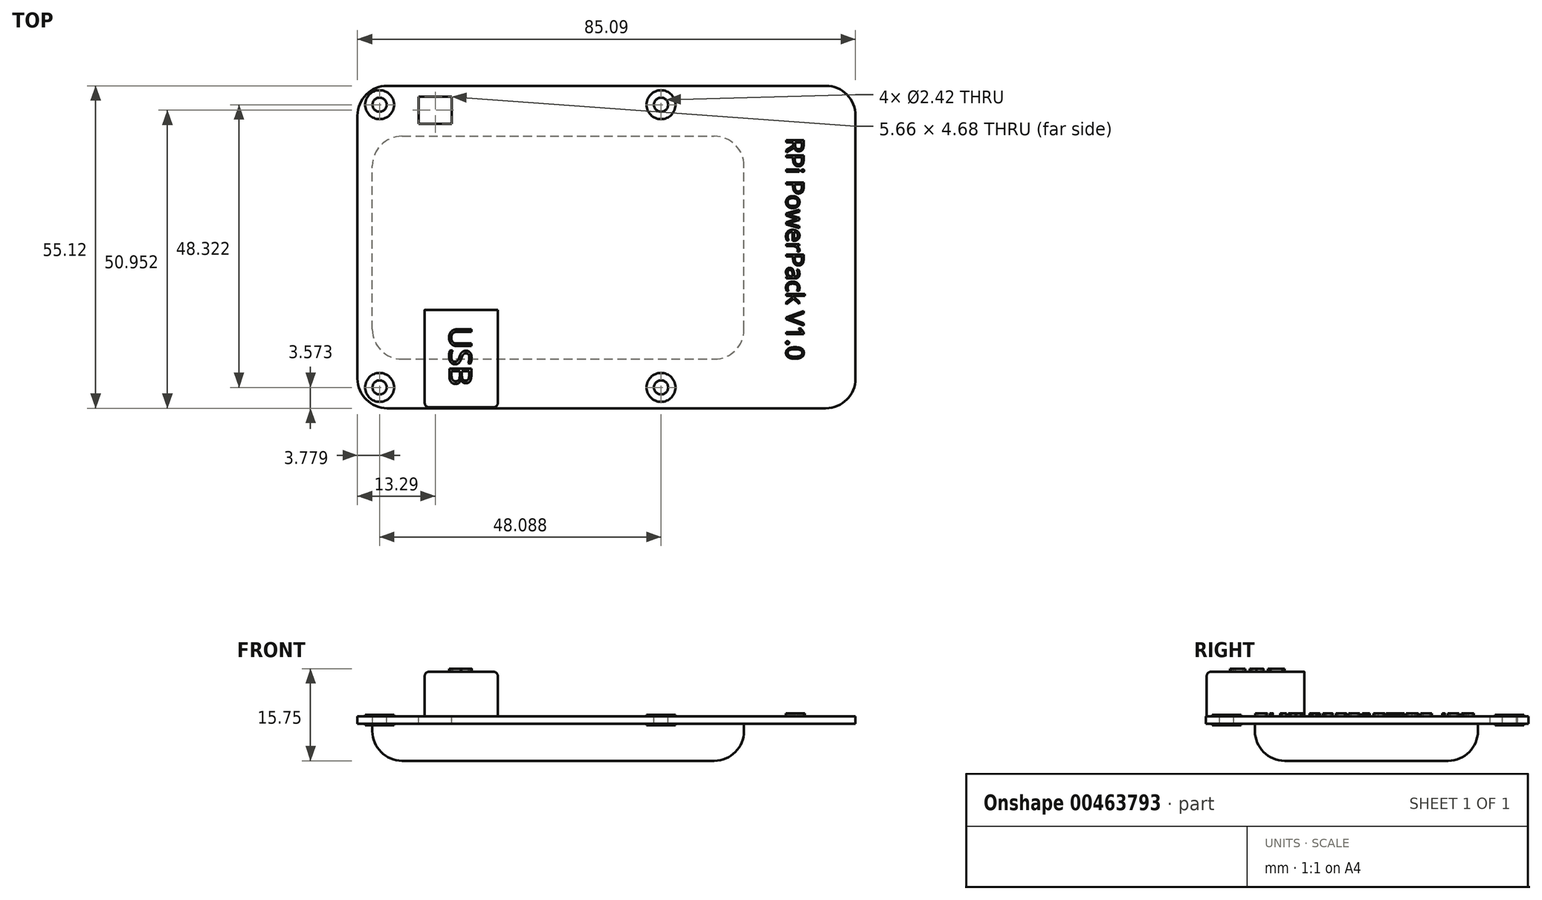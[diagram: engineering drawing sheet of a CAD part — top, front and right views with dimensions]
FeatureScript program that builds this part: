
annotation { "Feature Type Name" : "Feature", "Feature Type Description" : "" }
export const myFeature = defineFeature(function(context is Context, id is Id, definition is map)
    precondition{}
    {
        {
            var Q0;
            Q0=qCreatedBy(makeId("Top.planeOp"),FACE);
            var sketch = newSketch(context, id + "F0", { "sketchPlane" : qUnion([Q0])});
            skLineSegment(sketch, "E0.bottom", {"start": v(0, 0) * mm, "end": v(85.1, 0) * mm});
            skLineSegment(sketch, "E0.top", {"start": v(0, -55.12) * mm, "end": v(85.1, -55.12) * mm});
            skLineSegment(sketch, "E0.left", {"start": v(0, 0) * mm, "end": v(0, -55.12) * mm});
            skLineSegment(sketch, "E0.right", {"start": v(85.1, 0) * mm, "end": v(85.1, -55.12) * mm});
            skSolve(sketch);
        }
        {
            var Q0;
            Q0=makeQuery(id+"F0.imprint","IMPRINT",FACE,{"disambiguationData":[TD([[makeQuery(id+"F0.imprint","IMPRINT",EDGE,{"derivedFrom":sQuery(id+"F0.wireOp",EDGE,"E0.bottom")}),-1.0]])]});
            extrude(context, id + "F1", {"entities" : qUnion([Q0]), "depth" : 1.27 * mm});
        }
        {
            var Q0;
            Q0=makeQuery(id+"F1.opExtrude","SWEPT_EDGE",EDGE,{"disambiguationData":[OSD([sQuery(id+"F0.wireOp",EDGE,"E0.top"),sQuery(id+"F0.wireOp",EDGE,"E0.right")])]});
            var Q1;
            Q1=makeQuery(id+"F1.opExtrude","SWEPT_EDGE",EDGE,{"disambiguationData":[OSD([sQuery(id+"F0.wireOp",EDGE,"E0.top"),sQuery(id+"F0.wireOp",EDGE,"E0.left")])]});
            var Q2;
            Q2=makeQuery(id+"F1.opExtrude","SWEPT_EDGE",EDGE,{"disambiguationData":[OSD([sQuery(id+"F0.wireOp",EDGE,"E0.bottom"),sQuery(id+"F0.wireOp",EDGE,"E0.right")])]});
            var Q3;
            Q3=makeQuery(id+"F1.opExtrude","SWEPT_EDGE",EDGE,{"disambiguationData":[OSD([sQuery(id+"F0.wireOp",EDGE,"E0.bottom"),sQuery(id+"F0.wireOp",EDGE,"E0.left")])]});
            fillet(context, id + "F2", {"entities" : qUnion([Q0, Q1, Q2, Q3]), "radius" : 5.08 * mm, "tangentPropagation" : true, "allowEdgeOverflow" : false});
        }
        {
            var Q0;
            Q0=makeQuery(id+"F1.opExtrude","CAP_FACE",FACE,{"disambiguationData":[OSD([sQuery(id+"F0.wireOp",EDGE,"E0.bottom"),sQuery(id+"F0.wireOp",EDGE,"E0.top"),sQuery(id+"F0.wireOp",EDGE,"E0.left"),sQuery(id+"F0.wireOp",EDGE,"E0.right")])],"isStart":false});
            var sketch = newSketch(context, id + "F3", { "sketchPlane" : qUnion([Q0])});
            skCircle(sketch, "E1", {"center": v(51.87, -3.22) * mm, "radius": 2.47 * mm});
            skCircle(sketch, "E2", {"center": v(51.87, -51.55) * mm, "radius": 2.47 * mm});
            skCircle(sketch, "E3", {"center": v(3.78, -3.22) * mm, "radius": 2.47 * mm});
            skCircle(sketch, "E4", {"center": v(3.78, -51.55) * mm, "radius": 2.47 * mm});
            skCircle(sketch, "E5", {"center": v(51.87, -3.22) * mm, "radius": 1.21 * mm});
            skCircle(sketch, "E6", {"center": v(51.87, -51.55) * mm, "radius": 1.21 * mm});
            skCircle(sketch, "E7", {"center": v(3.78, -51.55) * mm, "radius": 1.21 * mm});
            skCircle(sketch, "E8", {"center": v(3.78, -3.22) * mm, "radius": 1.21 * mm});
            skSolve(sketch);
        }
        {
            var Q0;
            Q0=makeQuery(id+"F3.imprint","IMPRINT",FACE,{"disambiguationData":[TD([[makeQuery(id+"F3.imprint","IMPRINT",EDGE,{"derivedFrom":sQuery(id+"F3.wireOp",EDGE,"E5")}),1.0]])]});
            var Q1;
            Q1=makeQuery(id+"F3.imprint","IMPRINT",FACE,{"disambiguationData":[TD([[makeQuery(id+"F3.imprint","IMPRINT",EDGE,{"derivedFrom":sQuery(id+"F3.wireOp",EDGE,"E6")}),1.0]])]});
            var Q2;
            Q2=makeQuery(id+"F3.imprint","IMPRINT",FACE,{"disambiguationData":[TD([[makeQuery(id+"F3.imprint","IMPRINT",EDGE,{"derivedFrom":sQuery(id+"F3.wireOp",EDGE,"E8")}),1.0]])]});
            var Q3;
            Q3=makeQuery(id+"F3.imprint","IMPRINT",FACE,{"disambiguationData":[TD([[makeQuery(id+"F3.imprint","IMPRINT",EDGE,{"derivedFrom":sQuery(id+"F3.wireOp",EDGE,"E7")}),1.0]])]});
            extrude(context, id + "F4", {"entities" : qUnion([Q0, Q1, Q2, Q3]), "operationType" : NewBodyOperationType.REMOVE, "oppositeDirection" : true, "depth" : 1.27 * mm});
        }
        {
            var Q0;
            Q0=makeQuery(id+"F1.opExtrude","CAP_FACE",FACE,{"disambiguationData":[OSD([sQuery(id+"F0.wireOp",EDGE,"E0.bottom"),sQuery(id+"F0.wireOp",EDGE,"E0.top"),sQuery(id+"F0.wireOp",EDGE,"E0.left"),sQuery(id+"F0.wireOp",EDGE,"E0.right")])],"isStart":true});
            var sketch = newSketch(context, id + "F5", { "sketchPlane" : qUnion([Q0])});
            skLineSegment(sketch, "E9.bottom", {"start": v(2.54, 46.72) * mm, "end": v(66.04, 46.72) * mm});
            skLineSegment(sketch, "E9.top", {"start": v(2.54, 8.62) * mm, "end": v(66.04, 8.62) * mm});
            skLineSegment(sketch, "E9.left", {"start": v(2.54, 46.72) * mm, "end": v(2.54, 8.62) * mm});
            skLineSegment(sketch, "E9.right", {"start": v(66.04, 46.72) * mm, "end": v(66.04, 8.62) * mm});
            skSolve(sketch);
        }
        {
            var Q0;
            Q0=makeQuery(id+"F5.imprint","IMPRINT",FACE,{"disambiguationData":[TD([[makeQuery(id+"F5.imprint","IMPRINT",EDGE,{"derivedFrom":sQuery(id+"F5.wireOp",EDGE,"E9.bottom")}),-1.0]])]});
            extrude(context, id + "F6", {"entities" : qUnion([Q0]), "operationType" : NewBodyOperationType.ADD, "depth" : 6.35 * mm});
        }
        {
            var Q0;
            Q0=makeQuery(id+"F6.opExtrude","CAP_EDGE",EDGE,{"disambiguationData":[OSD([sQuery(id+"F5.wireOp",EDGE,"E9.top")])],"isStart":false});
            var Q1;
            Q1=makeQuery(id+"F6.opExtrude","CAP_EDGE",EDGE,{"disambiguationData":[OSD([sQuery(id+"F5.wireOp",EDGE,"E9.left")])],"isStart":false});
            var Q2;
            Q2=makeQuery(id+"F6.opExtrude","CAP_EDGE",EDGE,{"disambiguationData":[OSD([sQuery(id+"F5.wireOp",EDGE,"E9.bottom")])],"isStart":false});
            var Q3;
            Q3=makeQuery(id+"F6.opExtrude","CAP_EDGE",EDGE,{"disambiguationData":[OSD([sQuery(id+"F5.wireOp",EDGE,"E9.right")])],"isStart":false});
            fillet(context, id + "F7", {"entities" : qUnion([Q0, Q1, Q2, Q3]), "radius" : 5.08 * mm, "tangentPropagation" : true, "allowEdgeOverflow" : false});
        }
        {
            var Q0;
            Q0=makeQuery(id+"F7.opFillet","BLEND_EDGE",EDGE,{"blendedFrom":[makeQuery(id+"F6.opExtrude","CAP_EDGE",EDGE,{"disambiguationData":[OSD([sQuery(id+"F5.wireOp",EDGE,"E9.bottom")])],"isStart":false}),makeQuery(id+"F6.opExtrude","CAP_EDGE",EDGE,{"disambiguationData":[OSD([sQuery(id+"F5.wireOp",EDGE,"E9.left")])],"isStart":false})],"blendedInto":[]});
            var Q1;
            Q1=makeQuery(id+"F7.opFillet","BLEND_EDGE",EDGE,{"blendedFrom":[makeQuery(id+"F6.opExtrude","CAP_EDGE",EDGE,{"disambiguationData":[OSD([sQuery(id+"F5.wireOp",EDGE,"E9.bottom")])],"isStart":false}),makeQuery(id+"F6.opExtrude","CAP_EDGE",EDGE,{"disambiguationData":[OSD([sQuery(id+"F5.wireOp",EDGE,"E9.right")])],"isStart":false})],"blendedInto":[]});
            var Q2;
            Q2=makeQuery(id+"F7.opFillet","BLEND_EDGE",EDGE,{"blendedFrom":[makeQuery(id+"F6.opExtrude","CAP_EDGE",EDGE,{"disambiguationData":[OSD([sQuery(id+"F5.wireOp",EDGE,"E9.top")])],"isStart":false}),makeQuery(id+"F6.opExtrude","CAP_EDGE",EDGE,{"disambiguationData":[OSD([sQuery(id+"F5.wireOp",EDGE,"E9.right")])],"isStart":false})],"blendedInto":[]});
            var Q3;
            Q3=makeQuery(id+"F7.opFillet","BLEND_EDGE",EDGE,{"blendedFrom":[makeQuery(id+"F6.opExtrude","CAP_EDGE",EDGE,{"disambiguationData":[OSD([sQuery(id+"F5.wireOp",EDGE,"E9.top")])],"isStart":false}),makeQuery(id+"F6.opExtrude","CAP_EDGE",EDGE,{"disambiguationData":[OSD([sQuery(id+"F5.wireOp",EDGE,"E9.left")])],"isStart":false})],"blendedInto":[]});
            fillet(context, id + "F8", {"entities" : qUnion([Q0, Q1, Q2, Q3]), "radius" : 5.08 * mm, "tangentPropagation" : true, "allowEdgeOverflow" : false});
        }
        {
            var Q0;
            Q0=makeQuery(id+"F1.opExtrude","CAP_FACE",FACE,{"disambiguationData":[OSD([sQuery(id+"F0.wireOp",EDGE,"E0.bottom"),sQuery(id+"F0.wireOp",EDGE,"E0.top"),sQuery(id+"F0.wireOp",EDGE,"E0.left"),sQuery(id+"F0.wireOp",EDGE,"E0.right")])],"isStart":false});
            var sketch = newSketch(context, id + "F9", { "sketchPlane" : qUnion([Q0])});
            skLineSegment(sketch, "E10.bottom", {"start": v(16.12, -6.5) * mm, "end": v(10.46, -6.5) * mm});
            skLineSegment(sketch, "E10.top", {"start": v(16.12, -1.83) * mm, "end": v(10.46, -1.83) * mm});
            skLineSegment(sketch, "E10.left", {"start": v(16.12, -6.5) * mm, "end": v(16.12, -1.83) * mm});
            skLineSegment(sketch, "E10.right", {"start": v(10.46, -6.5) * mm, "end": v(10.46, -1.83) * mm});
            skSolve(sketch);
        }
        {
            var Q0;
            Q0=makeQuery(id+"F9.imprint","IMPRINT",FACE,{"disambiguationData":[TD([[makeQuery(id+"F9.imprint","IMPRINT",EDGE,{"derivedFrom":sQuery(id+"F9.wireOp",EDGE,"E10.bottom")}),-1.0]])]});
            extrude(context, id + "F10", {"entities" : qUnion([Q0]), "operationType" : NewBodyOperationType.REMOVE, "oppositeDirection" : true, "depth" : 5.08 * mm});
        }
        {
            var Q0;
            Q0=makeQuery(id+"F9.imprint","IMPRINT",FACE,{"disambiguationData":[TD([[makeQuery(id+"F9.imprint","IMPRINT",EDGE,{"derivedFrom":sQuery(id+"F9.wireOp",EDGE,"E10.bottom")}),1.0]])]});
            var sketch = newSketch(context, id + "F11", { "sketchPlane" : qUnion([Q0])});
            skLineSegment(sketch, "E11.bottom", {"start": v(11.49, -54.95) * mm, "end": v(23.97, -54.95) * mm});
            skLineSegment(sketch, "E11.top", {"start": v(11.49, -38.3) * mm, "end": v(23.97, -38.3) * mm});
            skLineSegment(sketch, "E11.left", {"start": v(11.49, -54.95) * mm, "end": v(11.49, -38.3) * mm});
            skLineSegment(sketch, "E11.right", {"start": v(23.97, -54.95) * mm, "end": v(23.97, -38.3) * mm});
            skSolve(sketch);
        }
        {
            var Q0;
            Q0=makeQuery(id+"F11.imprint","IMPRINT",FACE,{"disambiguationData":[TD([[makeQuery(id+"F11.imprint","IMPRINT",EDGE,{"derivedFrom":sQuery(id+"F11.wireOp",EDGE,"E11.bottom")}),1.0]])]});
            extrude(context, id + "F12", {"entities" : qUnion([Q0]), "operationType" : NewBodyOperationType.ADD, "depth" : 7.62 * mm});
        }
        {
            var Q0;
            Q0=makeQuery(id+"F9.imprint","IMPRINT",FACE,{"disambiguationData":[TD([[makeQuery(id+"F9.imprint","IMPRINT",EDGE,{"derivedFrom":sQuery(id+"F9.wireOp",EDGE,"E10.bottom")}),1.0]])]});
            var sketch = newSketch(context, id + "F13", { "sketchPlane" : qUnion([Q0])});
            skText(sketch, "E12", { "text": "RPi PowerPack V1.0", "fontName": "OpenSans-Regular.ttf"});
            const initialGuessF13  = {"E12": [0.07325, -0.00889, 0, -1, 0.003]};
            skSetInitialGuess(sketch, initialGuessF13);
            skSolve(sketch);
        }
        {
            var Q0;
            Q0=qSketchRegion(id+"F13",true);
            extrude(context, id + "F14", {"entities" : qUnion([Q0]), "operationType" : NewBodyOperationType.ADD, "depth" : 0.5 * mm});
        }
        {
            var Q0;
            Q0=makeQuery(id+"F12.opExtrude","CAP_EDGE",EDGE,{"disambiguationData":[OSD([sQuery(id+"F11.wireOp",EDGE,"E11.left")])],"isStart":false});
            var Q1;
            Q1=makeQuery(id+"F12.opExtrude","CAP_EDGE",EDGE,{"disambiguationData":[OSD([sQuery(id+"F11.wireOp",EDGE,"E11.right")])],"isStart":false});
            var Q2;
            Q2=makeQuery(id+"F12.opExtrude","CAP_EDGE",EDGE,{"disambiguationData":[OSD([sQuery(id+"F11.wireOp",EDGE,"E11.bottom")])],"isStart":false});
            var Q3;
            Q3=makeQuery(id+"F12.opExtrude","SWEPT_EDGE",EDGE,{"disambiguationData":[OSD([sQuery(id+"F11.wireOp",EDGE,"E11.bottom"),sQuery(id+"F11.wireOp",EDGE,"E11.right")])]});
            var Q4;
            Q4=makeQuery(id+"F12.opExtrude","SWEPT_EDGE",EDGE,{"disambiguationData":[OSD([sQuery(id+"F11.wireOp",EDGE,"E11.bottom"),sQuery(id+"F11.wireOp",EDGE,"E11.left")])]});
            fillet(context, id + "F15", {"entities" : qUnion([Q0, Q1, Q2, Q3, Q4]), "radius" : 0.76 * mm, "tangentPropagation" : true, "allowEdgeOverflow" : false});
        }
        {
            var Q0;
            Q0=makeQuery(id+"F12.opExtrude","CAP_FACE",FACE,{"disambiguationData":[OSD([sQuery(id+"F11.wireOp",EDGE,"E11.bottom"),sQuery(id+"F11.wireOp",EDGE,"E11.top"),sQuery(id+"F11.wireOp",EDGE,"E11.left"),sQuery(id+"F11.wireOp",EDGE,"E11.right")])],"isStart":false});
            var sketch = newSketch(context, id + "F16", { "sketchPlane" : qUnion([Q0])});
            skText(sketch, "E13", { "text": "USB", "fontName": "OpenSans-Regular.ttf"});
            const initialGuessF16  = {"E13": [0.0157, -0.04114, 0, -1, 0.00378]};
            skSetInitialGuess(sketch, initialGuessF16);
            skSolve(sketch);
        }
        {
            var Q0;
            Q0=qSketchRegion(id+"F16",true);
            extrude(context, id + "F17", {"entities" : qUnion([Q0]), "operationType" : NewBodyOperationType.ADD, "depth" : 0.5 * mm});
        }
        {
            var Q0;
            Q0 = qSketchRegion(id + "F3", true);
            extrude(context, id + "F18", {"entities" : qUnion([Q0]), "operationType" : NewBodyOperationType.ADD, "depth" : 0.25 * mm, "hasSecondDirection" : true, "secondDirectionOppositeDirection" : true, "secondDirectionDepth" : 1.52 * mm});
        }
    });
